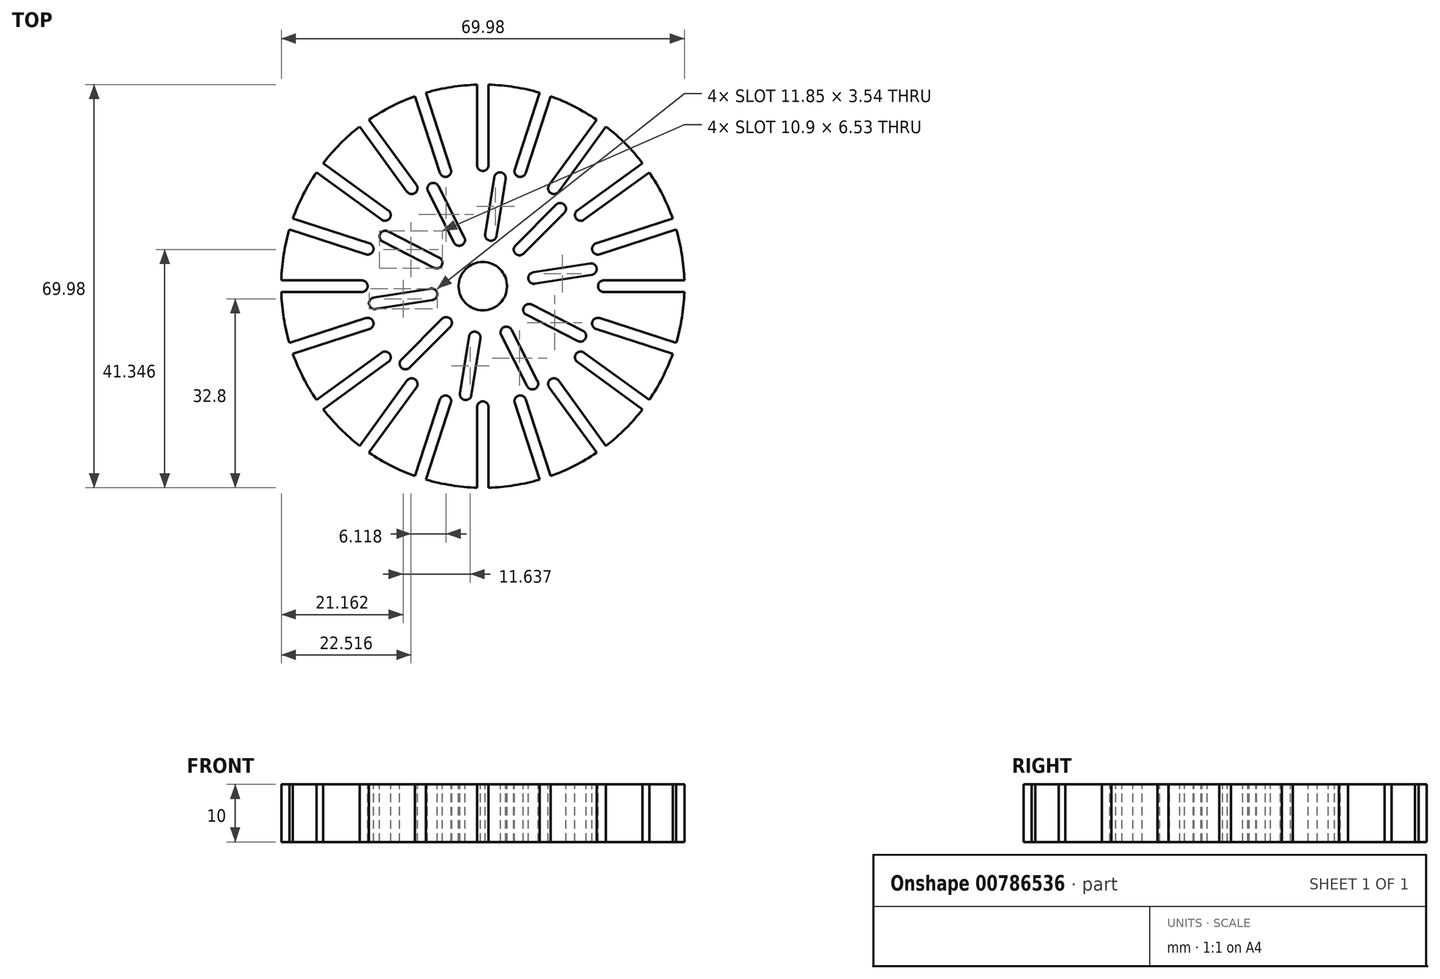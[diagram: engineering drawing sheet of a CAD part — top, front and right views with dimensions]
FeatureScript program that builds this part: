
annotation { "Feature Type Name" : "Feature", "Feature Type Description" : "" }
export const myFeature = defineFeature(function(context is Context, id is Id, definition is map)
    precondition{}
    {
        {
            var Q0;
            Q0=qCreatedBy(makeId("Top.planeOp"),FACE);
            var sketch = newSketch(context, id + "F0", { "sketchPlane" : qUnion([Q0])});
            skCircle(sketch, "E0", {"center": v(0, 0) * mm, "radius": 35 * mm});
            skSolve(sketch);
        }
        {
            var Q0;
            Q0 = qSketchRegion(id + "F0", true);
            extrude(context, id + "F1", {"entities" : qUnion([Q0]), "depth" : 10 * mm, "offsetDistance" : 25 * mm});
        }
        {
            var Q0;
            Q0=makeQuery(id+"F1.opExtrude","CAP_FACE",FACE,{"disambiguationData":[OSD([sQuery(id+"F0.wireOp",EDGE,"E0")])],"isStart":false});
            var sketch = newSketch(context, id + "F2", { "sketchPlane" : qUnion([Q0])});
            skCircle(sketch, "E1", {"center": v(0, 0) * mm, "radius": 4.2 * mm});
            skSolve(sketch);
        }
        {
            var Q0;
            Q0=makeQuery(id+"F2.imprint","IMPRINT",FACE,{"disambiguationData":[TD([[makeQuery(id+"F2.imprint","IMPRINT",EDGE,{"derivedFrom":sQuery(id+"F2.wireOp",EDGE,"E1")}),-1.0]])]});
            var sketch = newSketch(context, id + "F3", { "sketchPlane" : qUnion([Q0])});
            skLineSegment(sketch, "E2.bottom", {"start": v(-1, 35) * mm, "end": v(1, 35) * mm});
            skLineSegment(sketch, "E2.top", {"start": v(0, 20) * mm, "end": v(0, 20) * mm});
            skLineSegment(sketch, "E2.left", {"start": v(-1, 35) * mm, "end": v(-1, 21) * mm});
            skLineSegment(sketch, "E2.right", {"start": v(1, 35) * mm, "end": v(1, 21) * mm});
            skPoint(sketch, "E2.middle", {"position": v(0, 27.5) * mm});
            skPoint(sketch, "E3.visualSharp", {"position": v(-1, 20) * mm});
            skArc(sketch, "E3.filletArc", {"start": v(-1, 21) * mm, "mid": v(-0.7, 20.3) * mm, "end": v(0, 20) * mm});
            skPoint(sketch, "E4.visualSharp", {"position": v(1, 20) * mm});
            skArc(sketch, "E4.filletArc", {"start": v(0, 20) * mm, "mid": v(0.7, 20.3) * mm, "end": v(1, 21) * mm});
            skPoint(sketch, "E5.1.0", {"position": v(-8.5, 26.15) * mm});
            skPoint(sketch, "E5.1.1", {"position": v(-5.23, 19.33) * mm});
            skLineSegment(sketch, "E5.1.2", {"start": v(-11.77, 32.98) * mm, "end": v(-7.44, 19.66) * mm});
            skLineSegment(sketch, "E5.1.3", {"start": v(-9.86, 33.6) * mm, "end": v(-5.54, 20.28) * mm});
            skPoint(sketch, "E5.1.4", {"position": v(-7.13, 18.71) * mm});
            skLineSegment(sketch, "E5.1.5", {"start": v(-11.77, 32.98) * mm, "end": v(-9.86, 33.6) * mm});
            skArc(sketch, "E5.1.6", {"start": v(-7.44, 19.66) * mm, "mid": v(-6.94, 19.08) * mm, "end": v(-6.18, 19.02) * mm});
            skArc(sketch, "E5.1.7", {"start": v(-6.18, 19.02) * mm, "mid": v(-5.6, 19.52) * mm, "end": v(-5.54, 20.28) * mm});
            skPoint(sketch, "E5.2.0", {"position": v(-16.16, 22.25) * mm});
            skPoint(sketch, "E5.2.1", {"position": v(-10.95, 16.77) * mm});
            skLineSegment(sketch, "E5.2.2", {"start": v(-21.38, 27.73) * mm, "end": v(-13.15, 16.4) * mm});
            skLineSegment(sketch, "E5.2.3", {"start": v(-19.76, 28.9) * mm, "end": v(-11.53, 17.58) * mm});
            skPoint(sketch, "E5.2.4", {"position": v(-12.56, 15.6) * mm});
            skLineSegment(sketch, "E5.2.5", {"start": v(-21.38, 27.73) * mm, "end": v(-19.76, 28.9) * mm});
            skArc(sketch, "E5.2.6", {"start": v(-13.15, 16.4) * mm, "mid": v(-12.5, 16) * mm, "end": v(-11.76, 16.18) * mm});
            skArc(sketch, "E5.2.7", {"start": v(-11.76, 16.18) * mm, "mid": v(-11.36, 16.83) * mm, "end": v(-11.53, 17.58) * mm});
            skPoint(sketch, "E5.center", {"position": v(0, 0) * mm});
            skPoint(sketch, "E6.0.3.0", {"position": v(-16.77, 10.95) * mm});
            skPoint(sketch, "E6.1.3.0", {"position": v(-15.6, 12.56) * mm});
            skLineSegment(sketch, "E6.2.3.0", {"start": v(-28.9, 19.76) * mm, "end": v(-17.58, 11.53) * mm});
            skLineSegment(sketch, "E6.5.3.0", {"start": v(-27.73, 21.38) * mm, "end": v(-16.4, 13.15) * mm});
            skPoint(sketch, "E6.8.3.0", {"position": v(-22.25, 16.16) * mm});
            skLineSegment(sketch, "E6.9.3.0", {"start": v(-28.9, 19.76) * mm, "end": v(-27.73, 21.38) * mm});
            skArc(sketch, "E6.12.3.0", {"start": v(-17.58, 11.53) * mm, "mid": v(-16.83, 11.36) * mm, "end": v(-16.18, 11.76) * mm});
            skArc(sketch, "E6.16.3.0", {"start": v(-16.18, 11.76) * mm, "mid": v(-16, 12.5) * mm, "end": v(-16.4, 13.15) * mm});
            skPoint(sketch, "E6.0.4.0", {"position": v(-19.33, 5.23) * mm});
            skPoint(sketch, "E6.1.4.0", {"position": v(-18.71, 7.13) * mm});
            skLineSegment(sketch, "E6.2.4.0", {"start": v(-33.6, 9.86) * mm, "end": v(-20.28, 5.54) * mm});
            skLineSegment(sketch, "E6.5.4.0", {"start": v(-32.98, 11.77) * mm, "end": v(-19.66, 7.44) * mm});
            skPoint(sketch, "E6.8.4.0", {"position": v(-26.15, 8.5) * mm});
            skLineSegment(sketch, "E6.9.4.0", {"start": v(-33.6, 9.86) * mm, "end": v(-32.98, 11.77) * mm});
            skArc(sketch, "E6.12.4.0", {"start": v(-20.28, 5.54) * mm, "mid": v(-19.52, 5.6) * mm, "end": v(-19.02, 6.18) * mm});
            skArc(sketch, "E6.16.4.0", {"start": v(-19.02, 6.18) * mm, "mid": v(-19.08, 6.94) * mm, "end": v(-19.66, 7.44) * mm});
            skPoint(sketch, "E6.0.5.0", {"position": v(-20, -1) * mm});
            skPoint(sketch, "E6.1.5.0", {"position": v(-20, 1) * mm});
            skLineSegment(sketch, "E6.2.5.0", {"start": v(-35, -1) * mm, "end": v(-21, -1) * mm});
            skLineSegment(sketch, "E6.5.5.0", {"start": v(-35, 1) * mm, "end": v(-21, 1) * mm});
            skPoint(sketch, "E6.8.5.0", {"position": v(-27.5, 0) * mm});
            skLineSegment(sketch, "E6.9.5.0", {"start": v(-35, -1) * mm, "end": v(-35, 1) * mm});
            skArc(sketch, "E6.12.5.0", {"start": v(-21, -1) * mm, "mid": v(-20.3, -0.7) * mm, "end": v(-20, 0) * mm});
            skArc(sketch, "E6.16.5.0", {"start": v(-20, 0) * mm, "mid": v(-20.3, 0.7) * mm, "end": v(-21, 1) * mm});
            skPoint(sketch, "E6.0.6.0", {"position": v(-18.71, -7.13) * mm});
            skPoint(sketch, "E6.1.6.0", {"position": v(-19.33, -5.23) * mm});
            skLineSegment(sketch, "E6.2.6.0", {"start": v(-32.98, -11.77) * mm, "end": v(-19.66, -7.44) * mm});
            skLineSegment(sketch, "E6.5.6.0", {"start": v(-33.6, -9.86) * mm, "end": v(-20.28, -5.54) * mm});
            skPoint(sketch, "E6.8.6.0", {"position": v(-26.15, -8.5) * mm});
            skLineSegment(sketch, "E6.9.6.0", {"start": v(-32.98, -11.77) * mm, "end": v(-33.6, -9.86) * mm});
            skArc(sketch, "E6.12.6.0", {"start": v(-19.66, -7.44) * mm, "mid": v(-19.08, -6.94) * mm, "end": v(-19.02, -6.18) * mm});
            skArc(sketch, "E6.16.6.0", {"start": v(-19.02, -6.18) * mm, "mid": v(-19.52, -5.6) * mm, "end": v(-20.28, -5.54) * mm});
            skPoint(sketch, "E6.0.7.0", {"position": v(-15.6, -12.56) * mm});
            skPoint(sketch, "E6.1.7.0", {"position": v(-16.77, -10.95) * mm});
            skLineSegment(sketch, "E6.2.7.0", {"start": v(-27.73, -21.38) * mm, "end": v(-16.4, -13.15) * mm});
            skLineSegment(sketch, "E6.5.7.0", {"start": v(-28.9, -19.76) * mm, "end": v(-17.58, -11.53) * mm});
            skPoint(sketch, "E6.8.7.0", {"position": v(-22.25, -16.16) * mm});
            skLineSegment(sketch, "E6.9.7.0", {"start": v(-27.73, -21.38) * mm, "end": v(-28.9, -19.76) * mm});
            skArc(sketch, "E6.12.7.0", {"start": v(-16.4, -13.15) * mm, "mid": v(-16, -12.5) * mm, "end": v(-16.18, -11.76) * mm});
            skArc(sketch, "E6.16.7.0", {"start": v(-16.18, -11.76) * mm, "mid": v(-16.83, -11.36) * mm, "end": v(-17.58, -11.53) * mm});
            skPoint(sketch, "E6.0.8.0", {"position": v(-10.95, -16.77) * mm});
            skPoint(sketch, "E6.1.8.0", {"position": v(-12.56, -15.6) * mm});
            skLineSegment(sketch, "E6.2.8.0", {"start": v(-19.76, -28.9) * mm, "end": v(-11.53, -17.58) * mm});
            skLineSegment(sketch, "E6.5.8.0", {"start": v(-21.38, -27.73) * mm, "end": v(-13.15, -16.4) * mm});
            skPoint(sketch, "E6.8.8.0", {"position": v(-16.16, -22.25) * mm});
            skLineSegment(sketch, "E6.9.8.0", {"start": v(-19.76, -28.9) * mm, "end": v(-21.38, -27.73) * mm});
            skArc(sketch, "E6.12.8.0", {"start": v(-11.53, -17.58) * mm, "mid": v(-11.36, -16.83) * mm, "end": v(-11.76, -16.18) * mm});
            skArc(sketch, "E6.16.8.0", {"start": v(-11.76, -16.18) * mm, "mid": v(-12.5, -16) * mm, "end": v(-13.15, -16.4) * mm});
            skPoint(sketch, "E6.0.9.0", {"position": v(-5.23, -19.33) * mm});
            skPoint(sketch, "E6.1.9.0", {"position": v(-7.13, -18.71) * mm});
            skLineSegment(sketch, "E6.2.9.0", {"start": v(-9.86, -33.6) * mm, "end": v(-5.54, -20.28) * mm});
            skLineSegment(sketch, "E6.5.9.0", {"start": v(-11.77, -32.98) * mm, "end": v(-7.44, -19.66) * mm});
            skPoint(sketch, "E6.8.9.0", {"position": v(-8.5, -26.15) * mm});
            skLineSegment(sketch, "E6.9.9.0", {"start": v(-9.86, -33.6) * mm, "end": v(-11.77, -32.98) * mm});
            skArc(sketch, "E6.12.9.0", {"start": v(-5.54, -20.28) * mm, "mid": v(-5.6, -19.52) * mm, "end": v(-6.18, -19.02) * mm});
            skArc(sketch, "E6.16.9.0", {"start": v(-6.18, -19.02) * mm, "mid": v(-6.94, -19.08) * mm, "end": v(-7.44, -19.66) * mm});
            skPoint(sketch, "E7.0.10.0", {"position": v(1, -20) * mm});
            skPoint(sketch, "E7.1.10.0", {"position": v(-1, -20) * mm});
            skLineSegment(sketch, "E7.2.10.0", {"start": v(1, -35) * mm, "end": v(1, -21) * mm});
            skLineSegment(sketch, "E7.5.10.0", {"start": v(-1, -35) * mm, "end": v(-1, -21) * mm});
            skPoint(sketch, "E7.8.10.0", {"position": v(0, -27.5) * mm});
            skLineSegment(sketch, "E7.9.10.0", {"start": v(1, -35) * mm, "end": v(-1, -35) * mm});
            skArc(sketch, "E7.12.10.0", {"start": v(1, -21) * mm, "mid": v(0.7, -20.3) * mm, "end": v(0, -20) * mm});
            skArc(sketch, "E7.16.10.0", {"start": v(0, -20) * mm, "mid": v(-0.7, -20.3) * mm, "end": v(-1, -21) * mm});
            skPoint(sketch, "E7.0.11.0", {"position": v(7.13, -18.71) * mm});
            skPoint(sketch, "E7.1.11.0", {"position": v(5.23, -19.33) * mm});
            skLineSegment(sketch, "E7.2.11.0", {"start": v(11.77, -32.98) * mm, "end": v(7.44, -19.66) * mm});
            skLineSegment(sketch, "E7.5.11.0", {"start": v(9.86, -33.6) * mm, "end": v(5.54, -20.28) * mm});
            skPoint(sketch, "E7.8.11.0", {"position": v(8.5, -26.15) * mm});
            skLineSegment(sketch, "E7.9.11.0", {"start": v(11.77, -32.98) * mm, "end": v(9.86, -33.6) * mm});
            skArc(sketch, "E7.12.11.0", {"start": v(7.44, -19.66) * mm, "mid": v(6.94, -19.08) * mm, "end": v(6.18, -19.02) * mm});
            skArc(sketch, "E7.16.11.0", {"start": v(6.18, -19.02) * mm, "mid": v(5.6, -19.52) * mm, "end": v(5.54, -20.28) * mm});
            skPoint(sketch, "E7.0.12.0", {"position": v(12.56, -15.6) * mm});
            skPoint(sketch, "E7.1.12.0", {"position": v(10.95, -16.77) * mm});
            skLineSegment(sketch, "E7.2.12.0", {"start": v(21.38, -27.73) * mm, "end": v(13.15, -16.4) * mm});
            skLineSegment(sketch, "E7.5.12.0", {"start": v(19.76, -28.9) * mm, "end": v(11.53, -17.58) * mm});
            skPoint(sketch, "E7.8.12.0", {"position": v(16.16, -22.25) * mm});
            skLineSegment(sketch, "E7.9.12.0", {"start": v(21.38, -27.73) * mm, "end": v(19.76, -28.9) * mm});
            skArc(sketch, "E7.12.12.0", {"start": v(13.15, -16.4) * mm, "mid": v(12.5, -16) * mm, "end": v(11.76, -16.18) * mm});
            skArc(sketch, "E7.16.12.0", {"start": v(11.76, -16.18) * mm, "mid": v(11.36, -16.83) * mm, "end": v(11.53, -17.58) * mm});
            skPoint(sketch, "E7.0.13.0", {"position": v(16.77, -10.95) * mm});
            skPoint(sketch, "E7.1.13.0", {"position": v(15.6, -12.56) * mm});
            skLineSegment(sketch, "E7.2.13.0", {"start": v(28.9, -19.76) * mm, "end": v(17.58, -11.53) * mm});
            skLineSegment(sketch, "E7.5.13.0", {"start": v(27.73, -21.38) * mm, "end": v(16.4, -13.15) * mm});
            skPoint(sketch, "E7.8.13.0", {"position": v(22.25, -16.16) * mm});
            skLineSegment(sketch, "E7.9.13.0", {"start": v(28.9, -19.76) * mm, "end": v(27.73, -21.38) * mm});
            skArc(sketch, "E7.12.13.0", {"start": v(17.58, -11.53) * mm, "mid": v(16.83, -11.36) * mm, "end": v(16.18, -11.76) * mm});
            skArc(sketch, "E7.16.13.0", {"start": v(16.18, -11.76) * mm, "mid": v(16, -12.5) * mm, "end": v(16.4, -13.15) * mm});
            skPoint(sketch, "E7.0.14.0", {"position": v(19.33, -5.23) * mm});
            skPoint(sketch, "E7.1.14.0", {"position": v(18.71, -7.13) * mm});
            skLineSegment(sketch, "E7.2.14.0", {"start": v(33.6, -9.86) * mm, "end": v(20.28, -5.54) * mm});
            skLineSegment(sketch, "E7.5.14.0", {"start": v(32.98, -11.77) * mm, "end": v(19.66, -7.44) * mm});
            skPoint(sketch, "E7.8.14.0", {"position": v(26.15, -8.5) * mm});
            skLineSegment(sketch, "E7.9.14.0", {"start": v(33.6, -9.86) * mm, "end": v(32.98, -11.77) * mm});
            skArc(sketch, "E7.12.14.0", {"start": v(20.28, -5.54) * mm, "mid": v(19.52, -5.6) * mm, "end": v(19.02, -6.18) * mm});
            skArc(sketch, "E7.16.14.0", {"start": v(19.02, -6.18) * mm, "mid": v(19.08, -6.94) * mm, "end": v(19.66, -7.44) * mm});
            skPoint(sketch, "E7.0.15.0", {"position": v(20, 1) * mm});
            skPoint(sketch, "E7.1.15.0", {"position": v(20, -1) * mm});
            skLineSegment(sketch, "E7.2.15.0", {"start": v(35, 1) * mm, "end": v(21, 1) * mm});
            skLineSegment(sketch, "E7.5.15.0", {"start": v(35, -1) * mm, "end": v(21, -1) * mm});
            skPoint(sketch, "E7.8.15.0", {"position": v(27.5, 0) * mm});
            skLineSegment(sketch, "E7.9.15.0", {"start": v(35, 1) * mm, "end": v(35, -1) * mm});
            skArc(sketch, "E7.12.15.0", {"start": v(21, 1) * mm, "mid": v(20.3, 0.7) * mm, "end": v(20, 0) * mm});
            skArc(sketch, "E7.16.15.0", {"start": v(20, 0) * mm, "mid": v(20.3, -0.7) * mm, "end": v(21, -1) * mm});
            skPoint(sketch, "E7.0.16.0", {"position": v(18.71, 7.13) * mm});
            skPoint(sketch, "E7.1.16.0", {"position": v(19.33, 5.23) * mm});
            skLineSegment(sketch, "E7.2.16.0", {"start": v(32.98, 11.77) * mm, "end": v(19.66, 7.44) * mm});
            skLineSegment(sketch, "E7.5.16.0", {"start": v(33.6, 9.86) * mm, "end": v(20.28, 5.54) * mm});
            skPoint(sketch, "E7.8.16.0", {"position": v(26.15, 8.5) * mm});
            skLineSegment(sketch, "E7.9.16.0", {"start": v(32.98, 11.77) * mm, "end": v(33.6, 9.86) * mm});
            skArc(sketch, "E7.12.16.0", {"start": v(19.66, 7.44) * mm, "mid": v(19.08, 6.94) * mm, "end": v(19.02, 6.18) * mm});
            skArc(sketch, "E7.16.16.0", {"start": v(19.02, 6.18) * mm, "mid": v(19.52, 5.6) * mm, "end": v(20.28, 5.54) * mm});
            skPoint(sketch, "E7.0.17.0", {"position": v(15.6, 12.56) * mm});
            skPoint(sketch, "E7.1.17.0", {"position": v(16.77, 10.95) * mm});
            skLineSegment(sketch, "E7.2.17.0", {"start": v(27.73, 21.38) * mm, "end": v(16.4, 13.15) * mm});
            skLineSegment(sketch, "E7.5.17.0", {"start": v(28.9, 19.76) * mm, "end": v(17.58, 11.53) * mm});
            skPoint(sketch, "E7.8.17.0", {"position": v(22.25, 16.16) * mm});
            skLineSegment(sketch, "E7.9.17.0", {"start": v(27.73, 21.38) * mm, "end": v(28.9, 19.76) * mm});
            skArc(sketch, "E7.12.17.0", {"start": v(16.4, 13.15) * mm, "mid": v(16, 12.5) * mm, "end": v(16.18, 11.76) * mm});
            skArc(sketch, "E7.16.17.0", {"start": v(16.18, 11.76) * mm, "mid": v(16.83, 11.36) * mm, "end": v(17.58, 11.53) * mm});
            skPoint(sketch, "E7.0.18.0", {"position": v(10.95, 16.77) * mm});
            skPoint(sketch, "E7.1.18.0", {"position": v(12.56, 15.6) * mm});
            skLineSegment(sketch, "E7.2.18.0", {"start": v(19.76, 28.9) * mm, "end": v(11.53, 17.58) * mm});
            skLineSegment(sketch, "E7.5.18.0", {"start": v(21.38, 27.73) * mm, "end": v(13.15, 16.4) * mm});
            skPoint(sketch, "E7.8.18.0", {"position": v(16.16, 22.25) * mm});
            skLineSegment(sketch, "E7.9.18.0", {"start": v(19.76, 28.9) * mm, "end": v(21.38, 27.73) * mm});
            skArc(sketch, "E7.12.18.0", {"start": v(11.53, 17.58) * mm, "mid": v(11.36, 16.83) * mm, "end": v(11.76, 16.18) * mm});
            skArc(sketch, "E7.16.18.0", {"start": v(11.76, 16.18) * mm, "mid": v(12.5, 16) * mm, "end": v(13.15, 16.4) * mm});
            skPoint(sketch, "E7.0.19.0", {"position": v(5.23, 19.33) * mm});
            skPoint(sketch, "E7.1.19.0", {"position": v(7.13, 18.71) * mm});
            skLineSegment(sketch, "E7.2.19.0", {"start": v(9.86, 33.6) * mm, "end": v(5.54, 20.28) * mm});
            skLineSegment(sketch, "E7.5.19.0", {"start": v(11.77, 32.98) * mm, "end": v(7.44, 19.66) * mm});
            skPoint(sketch, "E7.8.19.0", {"position": v(8.5, 26.15) * mm});
            skLineSegment(sketch, "E7.9.19.0", {"start": v(9.86, 33.6) * mm, "end": v(11.77, 32.98) * mm});
            skArc(sketch, "E7.12.19.0", {"start": v(5.54, 20.28) * mm, "mid": v(5.6, 19.52) * mm, "end": v(6.18, 19.02) * mm});
            skArc(sketch, "E7.16.19.0", {"start": v(6.18, 19.02) * mm, "mid": v(6.94, 19.08) * mm, "end": v(7.44, 19.66) * mm});
            skSolve(sketch);
        }
        {
            var Q0;
            Q0 = qSketchRegion(id + "F3", true);
            var Q1;
            Q1=makeQuery(id+"F1.opExtrude","CAP_FACE",FACE,{"disambiguationData":[OSD([sQuery(id+"F0.wireOp",EDGE,"E0")])],"isStart":true});
            extrude(context, id + "F4", {"entities" : qUnion([Q0]), "operationType" : NewBodyOperationType.REMOVE, "endBound" : BoundingType.UP_TO_SURFACE, "oppositeDirection" : true, "depth" : 25 * mm, "endBoundEntityFace" : qUnion([Q1]), "offsetDistance" : 25 * mm});
        }
        {
            var Q0;
            Q0=makeQuery(id+"F2.imprint","IMPRINT",FACE,{"disambiguationData":[TD([[makeQuery(id+"F2.imprint","IMPRINT",EDGE,{"derivedFrom":sQuery(id+"F2.wireOp",EDGE,"E1")}),-1.0]])]});
            var sketch = newSketch(context, id + "F5", { "sketchPlane" : qUnion([Q0])});
            skLineSegment(sketch, "E8.bottom", {"start": v(3.13, 19.75) * mm, "end": v(3.13, 19.75) * mm});
            skLineSegment(sketch, "E8.top", {"start": v(1.25, 7.9) * mm, "end": v(1.25, 7.9) * mm});
            skLineSegment(sketch, "E8.left", {"start": v(2.4, 8.73) * mm, "end": v(3.96, 18.6) * mm});
            skLineSegment(sketch, "E8.right", {"start": v(0.42, 9.05) * mm, "end": v(1.98, 18.92) * mm});
            skLineSegment(sketch, "E9", {"start": v(0, 0) * mm, "end": v(1.25, 7.9) * mm, "construction": true});
            skPoint(sketch, "E10.visualSharp", {"position": v(2.14, 19.91) * mm});
            skArc(sketch, "E10.filletArc", {"start": v(3.13, 19.75) * mm, "mid": v(2.38, 19.58) * mm, "end": v(1.98, 18.92) * mm});
            skPoint(sketch, "E11.visualSharp", {"position": v(4.12, 19.6) * mm});
            skArc(sketch, "E11.filletArc", {"start": v(3.96, 18.6) * mm, "mid": v(3.78, 19.35) * mm, "end": v(3.13, 19.75) * mm});
            skPoint(sketch, "E12.visualSharp", {"position": v(0.26, 8.06) * mm});
            skArc(sketch, "E12.filletArc", {"start": v(0.42, 9.05) * mm, "mid": v(0.6, 8.3) * mm, "end": v(1.25, 7.9) * mm});
            skPoint(sketch, "E13.visualSharp", {"position": v(2.24, 7.75) * mm});
            skArc(sketch, "E13.filletArc", {"start": v(1.25, 7.9) * mm, "mid": v(2, 8.08) * mm, "end": v(2.4, 8.73) * mm});
            skLineSegment(sketch, "E14.1.0", {"start": v(-3.2, 8.47) * mm, "end": v(-7.73, 17.38) * mm});
            skLineSegment(sketch, "E14.1.1", {"start": v(-4.98, 7.57) * mm, "end": v(-9.52, 16.48) * mm});
            skPoint(sketch, "E14.1.2", {"position": v(-8.19, 18.27) * mm});
            skPoint(sketch, "E14.1.3", {"position": v(-2.74, 7.58) * mm});
            skPoint(sketch, "E14.1.4", {"position": v(-4.52, 6.67) * mm});
            skPoint(sketch, "E14.1.5", {"position": v(-9.97, 17.37) * mm});
            skArc(sketch, "E14.1.6", {"start": v(-4.98, 7.57) * mm, "mid": v(-4.4, 7.07) * mm, "end": v(-3.63, 7.13) * mm});
            skArc(sketch, "E14.1.7", {"start": v(-9.08, 17.82) * mm, "mid": v(-9.58, 17.24) * mm, "end": v(-9.52, 16.48) * mm});
            skArc(sketch, "E14.1.8", {"start": v(-3.63, 7.13) * mm, "mid": v(-3.13, 7.71) * mm, "end": v(-3.2, 8.47) * mm});
            skArc(sketch, "E14.1.9", {"start": v(-7.73, 17.38) * mm, "mid": v(-8.32, 17.88) * mm, "end": v(-9.08, 17.82) * mm});
            skLineSegment(sketch, "E14.2.0", {"start": v(-7.57, 4.98) * mm, "end": v(-16.48, 9.52) * mm});
            skLineSegment(sketch, "E14.2.1", {"start": v(-8.47, 3.2) * mm, "end": v(-17.38, 7.73) * mm});
            skPoint(sketch, "E14.2.2", {"position": v(-17.37, 9.97) * mm});
            skPoint(sketch, "E14.2.3", {"position": v(-6.67, 4.52) * mm});
            skPoint(sketch, "E14.2.4", {"position": v(-7.58, 2.74) * mm});
            skPoint(sketch, "E14.2.5", {"position": v(-18.27, 8.19) * mm});
            skArc(sketch, "E14.2.6", {"start": v(-8.47, 3.2) * mm, "mid": v(-7.71, 3.13) * mm, "end": v(-7.13, 3.63) * mm});
            skArc(sketch, "E14.2.7", {"start": v(-17.82, 9.08) * mm, "mid": v(-17.88, 8.32) * mm, "end": v(-17.38, 7.73) * mm});
            skArc(sketch, "E14.2.8", {"start": v(-7.13, 3.63) * mm, "mid": v(-7.07, 4.4) * mm, "end": v(-7.57, 4.98) * mm});
            skArc(sketch, "E14.2.9", {"start": v(-16.48, 9.52) * mm, "mid": v(-17.24, 9.58) * mm, "end": v(-17.82, 9.08) * mm});
            skPoint(sketch, "E14.center", {"position": v(0, 0) * mm});
            skPoint(sketch, "E15.0.3.0", {"position": v(-7.75, -2.24) * mm});
            skLineSegment(sketch, "E15.3.3.0", {"start": v(-8.73, -2.4) * mm, "end": v(-18.6, -3.96) * mm});
            skPoint(sketch, "E15.6.3.0", {"position": v(-19.91, -2.14) * mm});
            skPoint(sketch, "E15.7.3.0", {"position": v(-8.06, -0.26) * mm});
            skLineSegment(sketch, "E15.8.3.0", {"start": v(-9.05, -0.42) * mm, "end": v(-18.92, -1.98) * mm});
            skPoint(sketch, "E15.9.3.0", {"position": v(-19.6, -4.12) * mm});
            skArc(sketch, "E15.10.3.0", {"start": v(-8.73, -2.4) * mm, "mid": v(-8.08, -2) * mm, "end": v(-7.9, -1.25) * mm});
            skArc(sketch, "E15.14.3.0", {"start": v(-19.75, -3.13) * mm, "mid": v(-19.35, -3.78) * mm, "end": v(-18.6, -3.96) * mm});
            skArc(sketch, "E15.18.3.0", {"start": v(-7.9, -1.25) * mm, "mid": v(-8.3, -0.6) * mm, "end": v(-9.05, -0.42) * mm});
            skArc(sketch, "E15.22.3.0", {"start": v(-18.92, -1.98) * mm, "mid": v(-19.58, -2.38) * mm, "end": v(-19.75, -3.13) * mm});
            skPoint(sketch, "E15.0.4.0", {"position": v(-4.95, -6.36) * mm});
            skLineSegment(sketch, "E15.3.4.0", {"start": v(-5.66, -7.07) * mm, "end": v(-12.73, -14.14) * mm});
            skPoint(sketch, "E15.6.4.0", {"position": v(-14.85, -13.44) * mm});
            skPoint(sketch, "E15.7.4.0", {"position": v(-6.36, -4.95) * mm});
            skLineSegment(sketch, "E15.8.4.0", {"start": v(-7.07, -5.66) * mm, "end": v(-14.14, -12.73) * mm});
            skPoint(sketch, "E15.9.4.0", {"position": v(-13.44, -14.85) * mm});
            skArc(sketch, "E15.10.4.0", {"start": v(-5.66, -7.07) * mm, "mid": v(-5.36, -6.36) * mm, "end": v(-5.66, -5.66) * mm});
            skArc(sketch, "E15.14.4.0", {"start": v(-14.14, -14.14) * mm, "mid": v(-13.44, -14.44) * mm, "end": v(-12.73, -14.14) * mm});
            skArc(sketch, "E15.18.4.0", {"start": v(-5.66, -5.66) * mm, "mid": v(-6.36, -5.36) * mm, "end": v(-7.07, -5.66) * mm});
            skArc(sketch, "E15.22.4.0", {"start": v(-14.14, -12.73) * mm, "mid": v(-14.44, -13.44) * mm, "end": v(-14.14, -14.14) * mm});
            skPoint(sketch, "E15.0.5.0", {"position": v(-0.26, -8.06) * mm});
            skLineSegment(sketch, "E15.3.5.0", {"start": v(-0.42, -9.05) * mm, "end": v(-1.98, -18.92) * mm});
            skPoint(sketch, "E15.6.5.0", {"position": v(-4.12, -19.6) * mm});
            skPoint(sketch, "E15.7.5.0", {"position": v(-2.24, -7.75) * mm});
            skLineSegment(sketch, "E15.8.5.0", {"start": v(-2.4, -8.73) * mm, "end": v(-3.96, -18.6) * mm});
            skPoint(sketch, "E15.9.5.0", {"position": v(-2.14, -19.91) * mm});
            skArc(sketch, "E15.10.5.0", {"start": v(-0.42, -9.05) * mm, "mid": v(-0.6, -8.3) * mm, "end": v(-1.25, -7.9) * mm});
            skArc(sketch, "E15.14.5.0", {"start": v(-3.13, -19.75) * mm, "mid": v(-2.38, -19.58) * mm, "end": v(-1.98, -18.92) * mm});
            skArc(sketch, "E15.18.5.0", {"start": v(-1.25, -7.9) * mm, "mid": v(-2, -8.08) * mm, "end": v(-2.4, -8.73) * mm});
            skArc(sketch, "E15.22.5.0", {"start": v(-3.96, -18.6) * mm, "mid": v(-3.78, -19.35) * mm, "end": v(-3.13, -19.75) * mm});
            skPoint(sketch, "E15.0.6.0", {"position": v(4.52, -6.67) * mm});
            skLineSegment(sketch, "E15.3.6.0", {"start": v(4.98, -7.57) * mm, "end": v(9.52, -16.48) * mm});
            skPoint(sketch, "E15.6.6.0", {"position": v(8.19, -18.27) * mm});
            skPoint(sketch, "E15.7.6.0", {"position": v(2.74, -7.58) * mm});
            skLineSegment(sketch, "E15.8.6.0", {"start": v(3.2, -8.47) * mm, "end": v(7.73, -17.38) * mm});
            skPoint(sketch, "E15.9.6.0", {"position": v(9.97, -17.37) * mm});
            skArc(sketch, "E15.10.6.0", {"start": v(4.98, -7.57) * mm, "mid": v(4.4, -7.07) * mm, "end": v(3.63, -7.13) * mm});
            skArc(sketch, "E15.14.6.0", {"start": v(9.08, -17.82) * mm, "mid": v(9.58, -17.24) * mm, "end": v(9.52, -16.48) * mm});
            skArc(sketch, "E15.18.6.0", {"start": v(3.63, -7.13) * mm, "mid": v(3.13, -7.71) * mm, "end": v(3.2, -8.47) * mm});
            skArc(sketch, "E15.22.6.0", {"start": v(7.73, -17.38) * mm, "mid": v(8.32, -17.88) * mm, "end": v(9.08, -17.82) * mm});
            skPoint(sketch, "E15.0.7.0", {"position": v(7.58, -2.74) * mm});
            skLineSegment(sketch, "E15.3.7.0", {"start": v(8.47, -3.2) * mm, "end": v(17.38, -7.73) * mm});
            skPoint(sketch, "E15.6.7.0", {"position": v(17.37, -9.97) * mm});
            skPoint(sketch, "E15.7.7.0", {"position": v(6.67, -4.52) * mm});
            skLineSegment(sketch, "E15.8.7.0", {"start": v(7.57, -4.98) * mm, "end": v(16.48, -9.52) * mm});
            skPoint(sketch, "E15.9.7.0", {"position": v(18.27, -8.19) * mm});
            skArc(sketch, "E15.10.7.0", {"start": v(8.47, -3.2) * mm, "mid": v(7.71, -3.13) * mm, "end": v(7.13, -3.63) * mm});
            skArc(sketch, "E15.14.7.0", {"start": v(17.82, -9.08) * mm, "mid": v(17.88, -8.32) * mm, "end": v(17.38, -7.73) * mm});
            skArc(sketch, "E15.18.7.0", {"start": v(7.13, -3.63) * mm, "mid": v(7.07, -4.4) * mm, "end": v(7.57, -4.98) * mm});
            skArc(sketch, "E15.22.7.0", {"start": v(16.48, -9.52) * mm, "mid": v(17.24, -9.58) * mm, "end": v(17.82, -9.08) * mm});
            skPoint(sketch, "E15.0.8.0", {"position": v(7.75, 2.24) * mm});
            skLineSegment(sketch, "E15.3.8.0", {"start": v(8.73, 2.4) * mm, "end": v(18.6, 3.96) * mm});
            skPoint(sketch, "E15.6.8.0", {"position": v(19.91, 2.14) * mm});
            skPoint(sketch, "E15.7.8.0", {"position": v(8.06, 0.26) * mm});
            skLineSegment(sketch, "E15.8.8.0", {"start": v(9.05, 0.42) * mm, "end": v(18.92, 1.98) * mm});
            skPoint(sketch, "E15.9.8.0", {"position": v(19.6, 4.12) * mm});
            skArc(sketch, "E15.10.8.0", {"start": v(8.73, 2.4) * mm, "mid": v(8.08, 2) * mm, "end": v(7.9, 1.25) * mm});
            skArc(sketch, "E15.14.8.0", {"start": v(19.75, 3.13) * mm, "mid": v(19.35, 3.78) * mm, "end": v(18.6, 3.96) * mm});
            skArc(sketch, "E15.18.8.0", {"start": v(7.9, 1.25) * mm, "mid": v(8.3, 0.6) * mm, "end": v(9.05, 0.42) * mm});
            skArc(sketch, "E15.22.8.0", {"start": v(18.92, 1.98) * mm, "mid": v(19.58, 2.38) * mm, "end": v(19.75, 3.13) * mm});
            skPoint(sketch, "E15.0.9.0", {"position": v(4.95, 6.36) * mm});
            skLineSegment(sketch, "E15.3.9.0", {"start": v(5.66, 7.07) * mm, "end": v(12.73, 14.14) * mm});
            skPoint(sketch, "E15.6.9.0", {"position": v(14.85, 13.44) * mm});
            skPoint(sketch, "E15.7.9.0", {"position": v(6.36, 4.95) * mm});
            skLineSegment(sketch, "E15.8.9.0", {"start": v(7.07, 5.66) * mm, "end": v(14.14, 12.73) * mm});
            skPoint(sketch, "E15.9.9.0", {"position": v(13.44, 14.85) * mm});
            skArc(sketch, "E15.10.9.0", {"start": v(5.66, 7.07) * mm, "mid": v(5.36, 6.36) * mm, "end": v(5.66, 5.66) * mm});
            skArc(sketch, "E15.14.9.0", {"start": v(14.14, 14.14) * mm, "mid": v(13.44, 14.44) * mm, "end": v(12.73, 14.14) * mm});
            skArc(sketch, "E15.18.9.0", {"start": v(5.66, 5.66) * mm, "mid": v(6.36, 5.36) * mm, "end": v(7.07, 5.66) * mm});
            skArc(sketch, "E15.22.9.0", {"start": v(14.14, 12.73) * mm, "mid": v(14.44, 13.44) * mm, "end": v(14.14, 14.14) * mm});
            skSolve(sketch);
        }
        {
            var Q0;
            Q0 = qSketchRegion(id + "F5", true);
            var Q1;
            Q1=makeQuery(id+"F1.opExtrude","CAP_FACE",FACE,{"disambiguationData":[OSD([sQuery(id+"F0.wireOp",EDGE,"E0")])],"isStart":true});
            extrude(context, id + "F6", {"entities" : qUnion([Q0]), "operationType" : NewBodyOperationType.REMOVE, "endBound" : BoundingType.UP_TO_SURFACE, "oppositeDirection" : true, "depth" : 25 * mm, "endBoundEntityFace" : qUnion([Q1]), "offsetDistance" : 25 * mm});
        }
        {
            var Q0;
            Q0 = qSketchRegion(id + "F2", true);
            extrude(context, id + "F7", {"entities" : qUnion([Q0]), "operationType" : NewBodyOperationType.REMOVE, "endBound" : BoundingType.UP_TO_NEXT, "oppositeDirection" : true, "depth" : 25 * mm, "offsetDistance" : 25 * mm});
        }
    });
